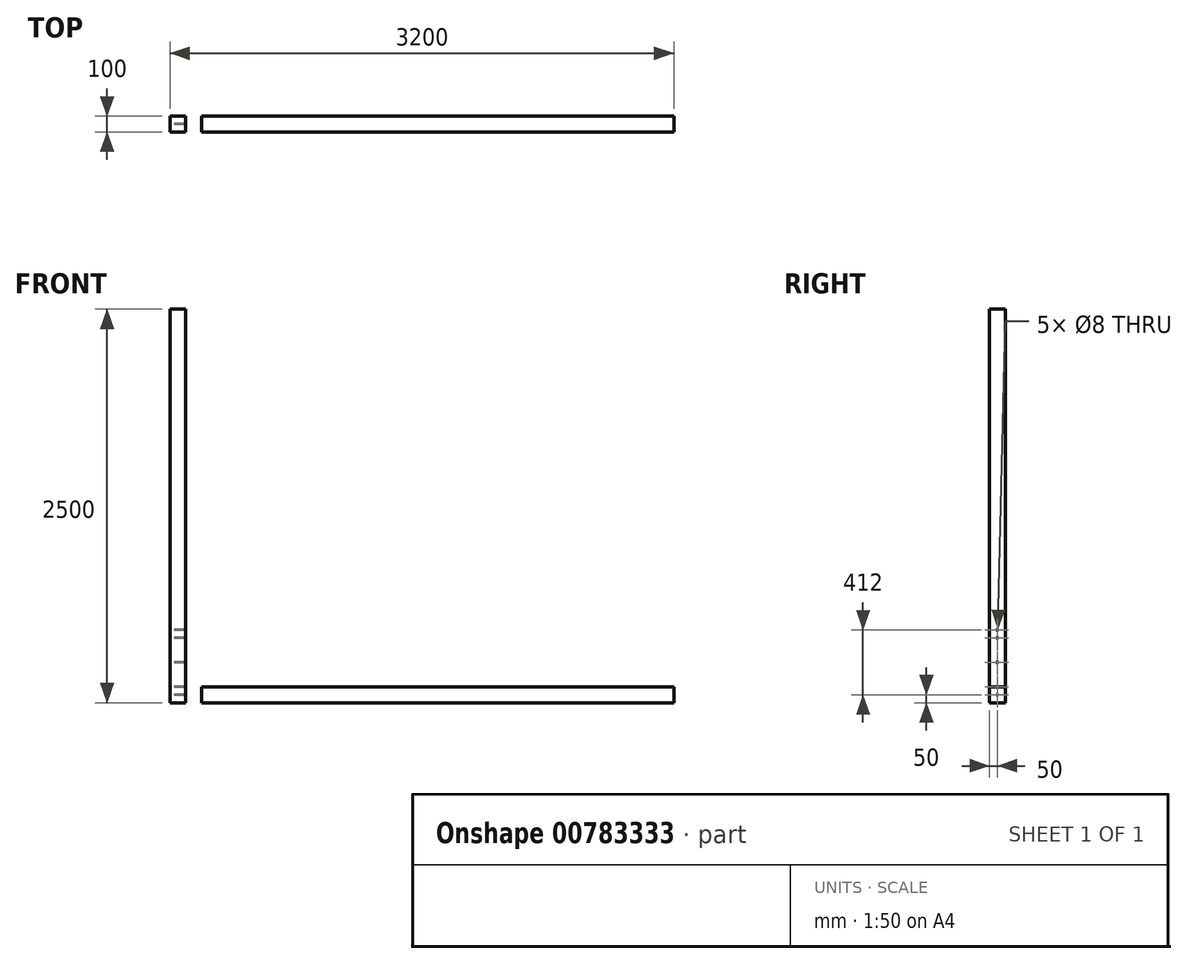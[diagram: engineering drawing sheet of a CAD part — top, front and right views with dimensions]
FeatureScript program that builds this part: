
annotation { "Feature Type Name" : "Feature", "Feature Type Description" : "" }
export const myFeature = defineFeature(function(context is Context, id is Id, definition is map)
    precondition{}
    {
        {
            var Q0;
            Q0=qCreatedBy(makeId("Top.planeOp"),FACE);
            var sketch = newSketch(context, id + "F0", { "sketchPlane" : qUnion([Q0])});
            skLineSegment(sketch, "E0.bottom", {"start": v(0, 0) * mm, "end": v(-100, 0) * mm});
            skLineSegment(sketch, "E0.top", {"start": v(0, 100) * mm, "end": v(-100, 100) * mm});
            skLineSegment(sketch, "E0.left", {"start": v(0, 0) * mm, "end": v(0, 100) * mm});
            skLineSegment(sketch, "E0.right", {"start": v(-100, 0) * mm, "end": v(-100, 100) * mm});
            skSolve(sketch);
        }
        {
            var Q0;
            Q0 = qSketchRegion(id + "F0", true);
            extrude(context, id + "F1", {"entities" : qUnion([Q0]), "depth" : 2500 * mm, "offsetDistance" : 25 * mm});
        }
        {
            var Q0;
            Q0=qCreatedBy(makeId("Top.planeOp"),FACE);
            var sketch = newSketch(context, id + "F2", { "sketchPlane" : qUnion([Q0])});
            skLineSegment(sketch, "E1.bottom", {"start": v(100, 0) * mm, "end": v(3100, 0) * mm});
            skLineSegment(sketch, "E1.top", {"start": v(100, 100) * mm, "end": v(3100, 100) * mm});
            skLineSegment(sketch, "E1.left", {"start": v(100, 0) * mm, "end": v(100, 100) * mm});
            skLineSegment(sketch, "E1.right", {"start": v(3100, 0) * mm, "end": v(3100, 100) * mm});
            skSolve(sketch);
        }
        {
            var Q0;
            Q0 = qSketchRegion(id + "F2", true);
            extrude(context, id + "F3", {"entities" : qUnion([Q0]), "operationType" : NewBodyOperationType.ADD, "depth" : 100 * mm, "offsetDistance" : 25 * mm});
        }
        {
            var Q0;
            Q0=makeQuery(id+"F1.opExtrude","SWEPT_FACE",FACE,{"disambiguationData":[OSD([sQuery(id+"F0.wireOp",EDGE,"E0.right")])]});
            var sketch = newSketch(context, id + "F4", { "sketchPlane" : qUnion([Q0])});
            skLineSegment(sketch, "E2", {"start": v(-50, 0) * mm, "end": v(-50, -40) * mm, "construction": true});
            skLineSegment(sketch, "E3", {"start": v(-50, -40) * mm, "end": v(-50, -48) * mm, "construction": true});
            skLineSegment(sketch, "E4", {"start": v(-50, -48) * mm, "end": v(-50, -88) * mm, "construction": true});
            skLineSegment(sketch, "E5", {"start": v(-100, 512) * mm, "end": v(0, 512) * mm, "construction": true});
            skLineSegment(sketch, "E6", {"start": v(-50, 512) * mm, "end": v(-50, 462) * mm, "construction": true});
            skLineSegment(sketch, "E7", {"start": v(-50, 462) * mm, "end": v(-50, 412) * mm, "construction": true});
            skLineSegment(sketch, "E8", {"start": v(-50, 412) * mm, "end": v(-50, 256) * mm, "construction": true});
            skLineSegment(sketch, "E9", {"start": v(-50, 256) * mm, "end": v(-50, 100) * mm, "construction": true});
            skLineSegment(sketch, "E10", {"start": v(-50, 100) * mm, "end": v(-50, 50) * mm, "construction": true});
            skLineSegment(sketch, "E11", {"start": v(-50, 50) * mm, "end": v(-50, 0) * mm, "construction": true});
            skSolve(sketch);
        }
        {
            var Q0;
            Q0=sQuery(id+"F4.wireOp",VERTEX,"E6.end");
            var Q1;
            Q1=sQuery(id+"F4.wireOp",VERTEX,"E7.end");
            var Q2;
            Q2=sQuery(id+"F4.wireOp",VERTEX,"E8.end");
            var Q3;
            Q3=sQuery(id+"F4.wireOp",VERTEX,"E9.end");
            var Q4;
            Q4=sQuery(id+"F4.wireOp",VERTEX,"E10.end");
            var Q5;
            Q5=makeQuery(id+"F1.opExtrude","SWEPT_BODY",BODY,{"disambiguationData":[OSD([sQuery(id+"F0.wireOp",EDGE,"E0.bottom"),sQuery(id+"F0.wireOp",EDGE,"E0.top"),sQuery(id+"F0.wireOp",EDGE,"E0.left"),sQuery(id+"F0.wireOp",EDGE,"E0.right")])]});
            hole(context, id + "F5", {"style" : HoleStyle.C_SINK, "endStyle" : HoleEndStyle.THROUGH, "holeDiameter" : 8 * mm, "cSinkDiameter" : 15 * mm, "cSinkAngle" : 90 * degree, "majorDiameter" : 5 * mm, "isTappedThrough" : true, "tappedDepth" : 12 * mm, "tapClearance" : 3, "locations" : qUnion([Q0, Q1, Q2, Q3, Q4]), "scope" : qUnion([Q5])});
        }
    });
